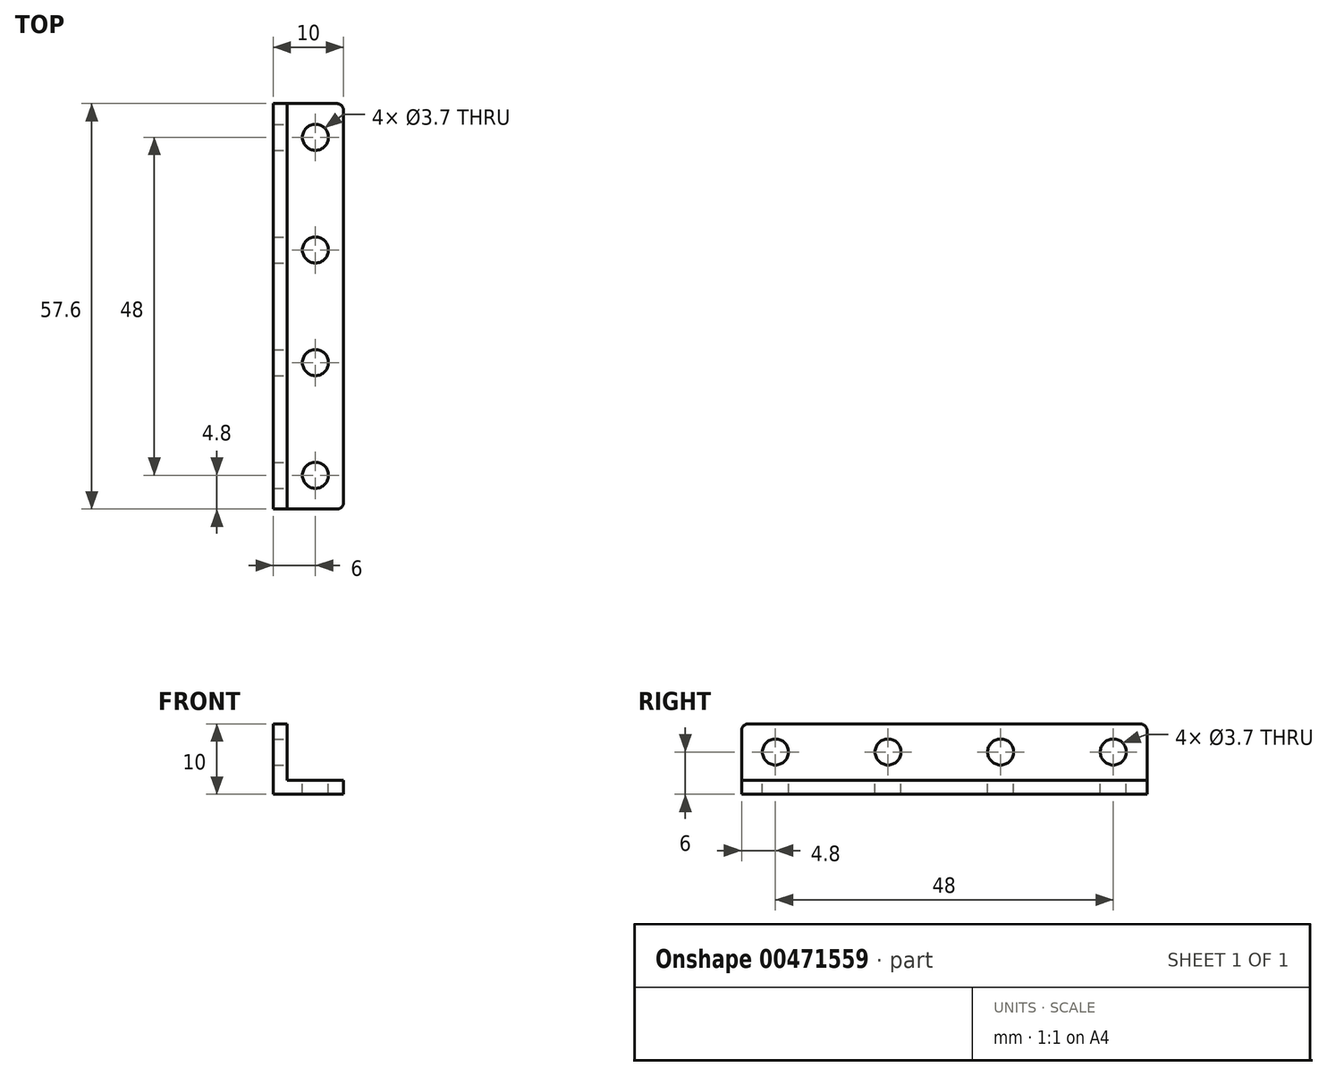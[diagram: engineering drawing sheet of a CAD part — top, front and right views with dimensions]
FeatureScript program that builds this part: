
annotation { "Feature Type Name" : "Feature", "Feature Type Description" : "" }
export const myFeature = defineFeature(function(context is Context, id is Id, definition is map)
    precondition{}
    {
        {
            var Q0;
            Q0=qCreatedBy(makeId("Front.planeOp"),FACE);
            var sketch = newSketch(context, id + "F0", { "sketchPlane" : qUnion([Q0])});
            skLineSegment(sketch, "E0.top", {"start": v(0, 8) * mm, "end": v(2, 8) * mm});
            skLineSegment(sketch, "E0.right", {"start": v(2, 0) * mm, "end": v(2, 8) * mm});
            skLineSegment(sketch, "E1.top", {"start": v(0, -2) * mm, "end": v(10, -2) * mm});
            skLineSegment(sketch, "E1.right", {"start": v(10, 0) * mm, "end": v(10, -2) * mm});
            skLineSegment(sketch, "E2", {"start": v(2, 0) * mm, "end": v(10, 0) * mm});
            skLineSegment(sketch, "E3", {"start": v(0, 8) * mm, "end": v(0, -2) * mm});
            skSolve(sketch);
        }
        {
            var Q0;
            Q0=makeQuery(id+"F0.imprint","IMPRINT",FACE,{"disambiguationData":[TD([[makeQuery(id+"F0.imprint","IMPRINT",EDGE,{"derivedFrom":sQuery(id+"F0.wireOp",EDGE,"E0.top")}),-1.0]])]});
            extrude(context, id + "F1", {"entities" : qUnion([Q0]), "depth" : 57.6 * mm});
        }
        {
            var Q0;
            Q0=makeQuery(id+"F1.opExtrude","CAP_EDGE",EDGE,{"disambiguationData":[OSD([sQuery(id+"F0.wireOp",EDGE,"E0.top")])],"isStart":false});
            fillet(context, id + "F2", {"entities" : qUnion([Q0]), "radius" : 1 * mm, "tangentPropagation" : true, "allowEdgeOverflow" : false});
        }
        {
            var Q0;
            Q0=makeQuery(id+"F1.opExtrude","CAP_EDGE",EDGE,{"disambiguationData":[OSD([sQuery(id+"F0.wireOp",EDGE,"E1.right")])],"isStart":false});
            fillet(context, id + "F3", {"entities" : qUnion([Q0]), "radius" : 1 * mm, "tangentPropagation" : true, "allowEdgeOverflow" : false});
        }
        {
            var Q0;
            Q0=makeQuery(id+"F1.opExtrude","CAP_EDGE",EDGE,{"disambiguationData":[OSD([sQuery(id+"F0.wireOp",EDGE,"E0.top")])],"isStart":true});
            fillet(context, id + "F4", {"entities" : qUnion([Q0]), "radius" : 1 * mm, "tangentPropagation" : true, "allowEdgeOverflow" : false});
        }
        {
            var Q0;
            Q0=makeQuery(id+"F1.opExtrude","CAP_EDGE",EDGE,{"disambiguationData":[OSD([sQuery(id+"F0.wireOp",EDGE,"E1.right")])],"isStart":true});
            fillet(context, id + "F5", {"entities" : qUnion([Q0]), "radius" : 1 * mm, "tangentPropagation" : true, "allowEdgeOverflow" : false});
        }
        {
            var Q0;
            Q0=makeQuery(id+"F1.opExtrude","SWEPT_FACE",FACE,{"disambiguationData":[OSD([sQuery(id+"F0.wireOp",EDGE,"E2")])]});
            var sketch = newSketch(context, id + "F6", { "sketchPlane" : qUnion([Q0])});
            skCircle(sketch, "E4", {"center": v(6, -52.8) * mm, "radius": 1.85 * mm});
            skLineSegment(sketch, "E5", {"start": v(6, -52.8) * mm, "end": v(2, -52.8) * mm});
            skLineSegment(sketch, "E6", {"start": v(6, -52.8) * mm, "end": v(6, -57.6) * mm});
            skLineSegment(sketch, "E7", {"start": v(6, -52.8) * mm, "end": v(6, -36.8) * mm});
            skLineSegment(sketch, "E8", {"start": v(6, -36.8) * mm, "end": v(6, -20.8) * mm});
            skLineSegment(sketch, "E9", {"start": v(6, -20.8) * mm, "end": v(6, -4.8) * mm});
            skCircle(sketch, "E10", {"center": v(6, -4.8) * mm, "radius": 1.85 * mm});
            skCircle(sketch, "E11", {"center": v(6, -20.8) * mm, "radius": 1.85 * mm});
            skCircle(sketch, "E12", {"center": v(6, -36.8) * mm, "radius": 1.85 * mm});
            skLineSegment(sketch, "E13", {"start": v(6, -4.8) * mm, "end": v(6, 0) * mm});
            skSolve(sketch);
        }
        {
            var Q0;
            Q0=sQuery(id+"F6.wireOp",VERTEX,"E5.start");
            var Q1;
            Q1=sQuery(id+"F6.wireOp",VERTEX,"E8.start");
            var Q2;
            Q2=sQuery(id+"F6.wireOp",VERTEX,"E9.start");
            var Q3;
            Q3=sQuery(id+"F6.wireOp",VERTEX,"E13.start");
            var Q4;
            Q4=makeQuery(id+"F1.opExtrude","SWEPT_BODY",BODY,{"disambiguationData":[OSD([sQuery(id+"F0.wireOp",EDGE,"E0.top"),sQuery(id+"F0.wireOp",EDGE,"E0.right"),sQuery(id+"F0.wireOp",EDGE,"E1.top"),sQuery(id+"F0.wireOp",EDGE,"E1.right"),sQuery(id+"F0.wireOp",EDGE,"E2"),sQuery(id+"F0.wireOp",EDGE,"E3")])]});
            hole(context, id + "F7", {"style" : HoleStyle.SIMPLE, "endStyle" : HoleEndStyle.THROUGH, "holeDiameter" : 3.7 * mm, "isTappedThrough" : true, "tappedDepth" : 12 * mm, "tapClearance" : 3, "locations" : qUnion([Q0, Q1, Q2, Q3]), "scope" : qUnion([Q4])});
        }
        {
            var Q0;
            Q0=makeQuery(id+"F1.opExtrude","SWEPT_FACE",FACE,{"disambiguationData":[OSD([sQuery(id+"F0.wireOp",EDGE,"E0.right")])]});
            var sketch = newSketch(context, id + "F8", { "sketchPlane" : qUnion([Q0])});
            skCircle(sketch, "E14", {"center": v(-52.8, 4) * mm, "radius": 1.85 * mm});
            skLineSegment(sketch, "E15", {"start": v(-52.8, 4) * mm, "end": v(-52.8, 8) * mm});
            skLineSegment(sketch, "E16", {"start": v(-52.8, 4) * mm, "end": v(-57.6, 4) * mm});
            skLineSegment(sketch, "E17", {"start": v(-52.8, 4) * mm, "end": v(-36.8, 4) * mm});
            skLineSegment(sketch, "E18", {"start": v(-36.8, 4) * mm, "end": v(-20.8, 4) * mm});
            skLineSegment(sketch, "E19", {"start": v(-20.8, 4) * mm, "end": v(-4.8, 4) * mm});
            skCircle(sketch, "E20", {"center": v(-36.8, 4) * mm, "radius": 1.85 * mm});
            skCircle(sketch, "E21", {"center": v(-20.8, 4) * mm, "radius": 1.85 * mm});
            skCircle(sketch, "E22", {"center": v(-4.8, 4) * mm, "radius": 1.85 * mm});
            skSolve(sketch);
        }
        {
            var Q0;
            Q0=sQuery(id+"F8.wireOp",VERTEX,"E14.center");
            var Q1;
            Q1=sQuery(id+"F8.wireOp",VERTEX,"E20.center");
            var Q2;
            Q2=sQuery(id+"F8.wireOp",VERTEX,"E21.center");
            var Q3;
            Q3=sQuery(id+"F8.wireOp",VERTEX,"E19.end");
            var Q4;
            Q4=makeQuery(id+"F1.opExtrude","SWEPT_BODY",BODY,{"disambiguationData":[OSD([sQuery(id+"F0.wireOp",EDGE,"E0.top"),sQuery(id+"F0.wireOp",EDGE,"E0.right"),sQuery(id+"F0.wireOp",EDGE,"E1.top"),sQuery(id+"F0.wireOp",EDGE,"E1.right"),sQuery(id+"F0.wireOp",EDGE,"E2"),sQuery(id+"F0.wireOp",EDGE,"E3")])]});
            hole(context, id + "F9", {"style" : HoleStyle.SIMPLE, "endStyle" : HoleEndStyle.THROUGH, "holeDiameter" : 3.7 * mm, "isTappedThrough" : true, "tappedDepth" : 12 * mm, "tapClearance" : 3, "locations" : qUnion([Q0, Q1, Q2, Q3]), "scope" : qUnion([Q4])});
        }
    });
